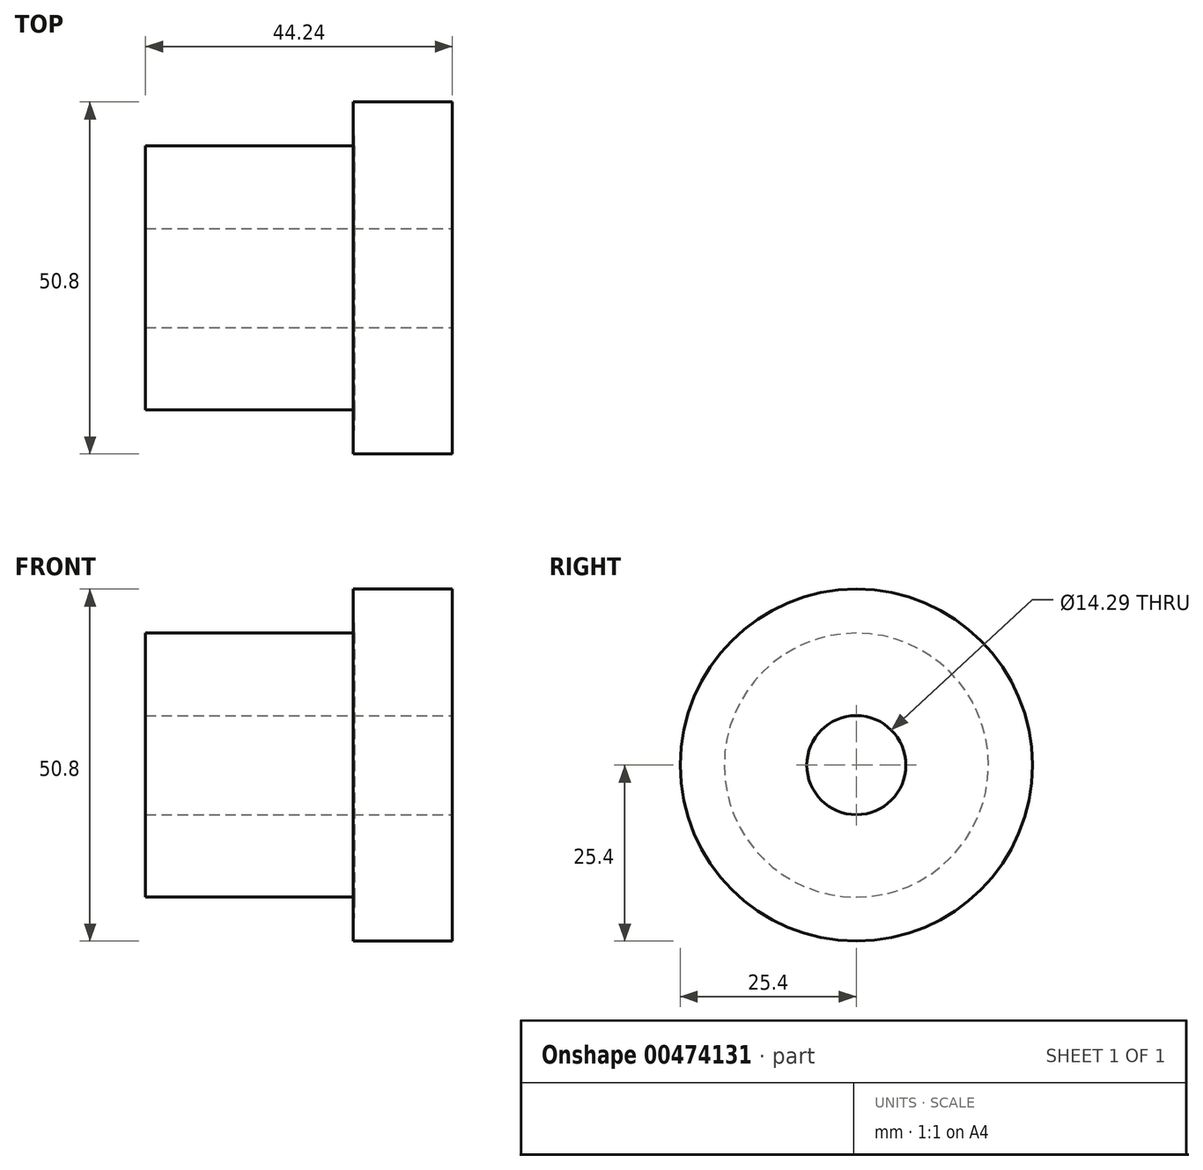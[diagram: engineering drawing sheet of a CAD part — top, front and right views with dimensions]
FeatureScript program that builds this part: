
annotation { "Feature Type Name" : "Feature", "Feature Type Description" : "" }
export const myFeature = defineFeature(function(context is Context, id is Id, definition is map)
    precondition{}
    {
        {
            var Q0;
            Q0=qCreatedBy(makeId("Front.planeOp"),FACE);
            var sketch = newSketch(context, id + "F0", { "sketchPlane" : qUnion([Q0])});
            skLineSegment(sketch, "E0", {"start": v(-19.93, 0) * mm, "end": v(24.31, 0) * mm});
            skLineSegment(sketch, "E1", {"start": v(-19.93, 0) * mm, "end": v(-19.93, 19.05) * mm});
            skLineSegment(sketch, "E2", {"start": v(-19.93, 19.05) * mm, "end": v(10.24, 19.05) * mm});
            skLineSegment(sketch, "E3", {"start": v(10.24, 19.05) * mm, "end": v(10.24, 0) * mm});
            skLineSegment(sketch, "E4", {"start": v(10.24, 0) * mm, "end": v(24.31, 0) * mm});
            skLineSegment(sketch, "E5", {"start": v(24.31, 0) * mm, "end": v(24.31, 25.4) * mm});
            skLineSegment(sketch, "E6", {"start": v(24.31, 25.4) * mm, "end": v(10.02, 25.4) * mm});
            skLineSegment(sketch, "E7", {"start": v(10.02, 25.4) * mm, "end": v(10.24, 19.05) * mm});
            skSolve(sketch);
        }
        {
            var Q0;
            Q0=makeQuery(id+"F0.imprint","IMPRINT",FACE,{"disambiguationData":[TD([[makeQuery(id+"F0.imprint","IMPRINT",EDGE,{"derivedFrom":sQuery(id+"F0.wireOp",EDGE,"E0")}),1.0]])]});
            var Q1;
            Q1=makeQuery(id+"F0.imprint","IMPRINT",FACE,{"disambiguationData":[TD([[makeQuery(id+"F0.imprint","IMPRINT",EDGE,{"derivedFrom":sQuery(id+"F0.wireOp",EDGE,"E3")}),1.0]])]});
            var Q2;
            Q2=sQuery(id+"F0.wireOp",EDGE,"E0");
            revolve(context, id + "F1", {"entities" : qUnion([Q0, Q1]), "axis" : qUnion([Q2]), "revolveType" : RevolveType.ONE_DIRECTION, "angle" : 360 * degree});
        }
        {
            var Q0;
            Q0=makeQuery(id+"F1.opRevolve","SWEPT_FACE",FACE,{"disambiguationData":[OSD([sQuery(id+"F0.wireOp",EDGE,"E5")])]});
            var sketch = newSketch(context, id + "F2", { "sketchPlane" : qUnion([Q0])});
            skCircle(sketch, "E8", {"center": v(0, 0) * mm, "radius": 7.14 * mm});
            skSolve(sketch);
        }
        {
            var Q0;
            Q0 = qSketchRegion(id + "F2", true);
            extrude(context, id + "F3", {"entities" : qUnion([Q0]), "operationType" : NewBodyOperationType.REMOVE, "endBound" : BoundingType.THROUGH_ALL, "oppositeDirection" : true, "depth" : 25.4 * mm});
        }
    });
